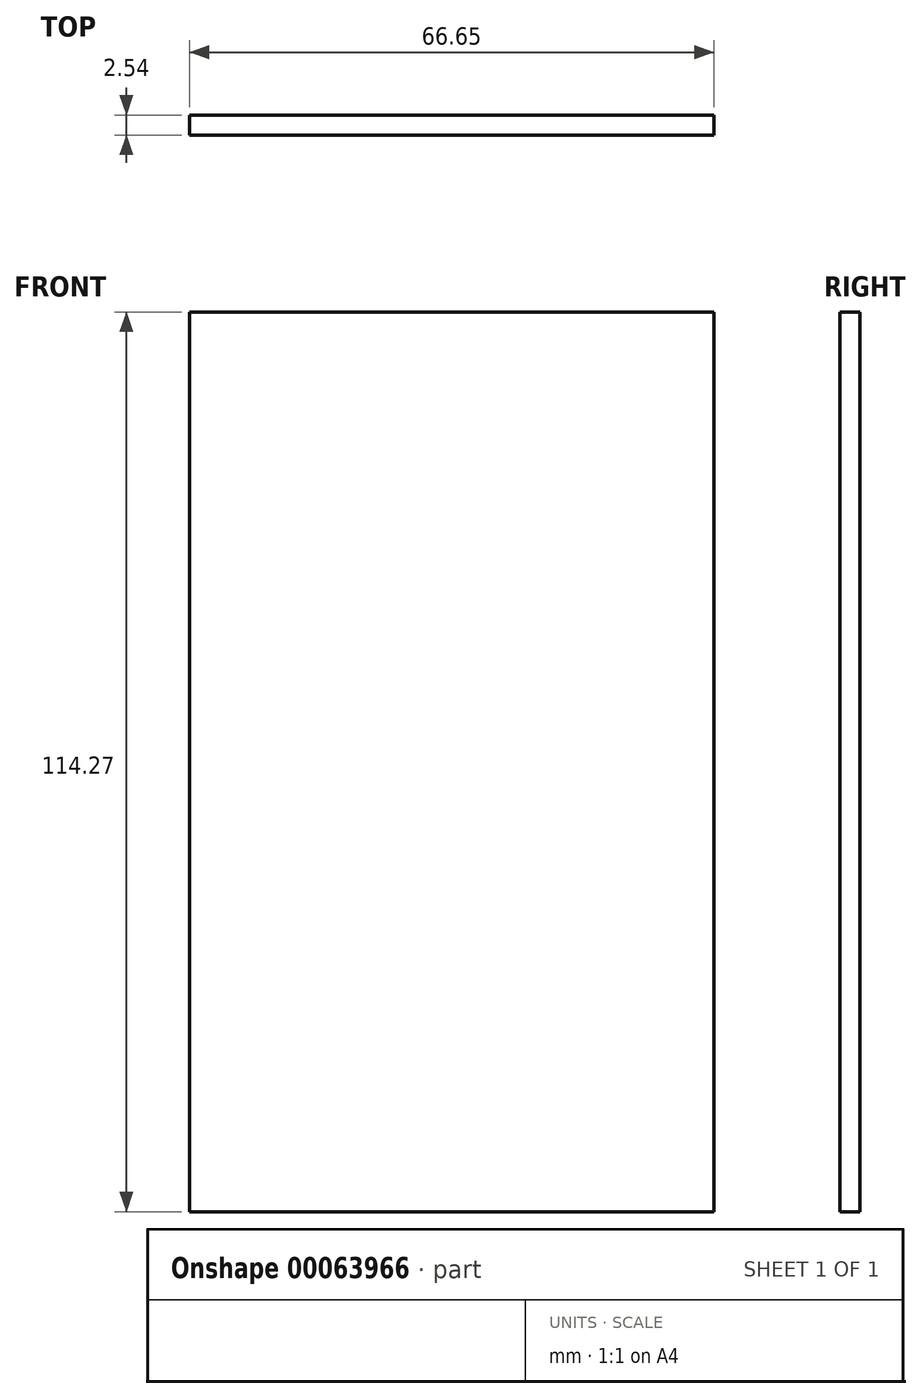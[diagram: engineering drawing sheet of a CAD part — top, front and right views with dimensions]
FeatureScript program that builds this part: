
annotation { "Feature Type Name" : "Feature", "Feature Type Description" : "" }
export const myFeature = defineFeature(function(context is Context, id is Id, definition is map)
    precondition{}
    {
        {
            var Q0;
            Q0=qCreatedBy(makeId("Front.planeOp"),FACE);
            var sketch = newSketch(context, id + "F0", { "sketchPlane" : qUnion([Q0])});
            skLineSegment(sketch, "E0.bottom", {"start": v(-38.79, 58.08) * mm, "end": v(27.86, 58.08) * mm});
            skLineSegment(sketch, "E0.top", {"start": v(-38.79, -56.19) * mm, "end": v(27.86, -56.19) * mm});
            skLineSegment(sketch, "E0.left", {"start": v(-38.79, 58.08) * mm, "end": v(-38.79, -56.19) * mm});
            skLineSegment(sketch, "E0.right", {"start": v(27.86, 58.08) * mm, "end": v(27.86, -56.19) * mm});
            skSolve(sketch);
        }
        {
            var Q0;
            Q0 = qSketchRegion(id + "F0", true);
            extrude(context, id + "F1", {"entities" : qUnion([Q0]), "depth" : 2.54 * mm});
        }
    });
